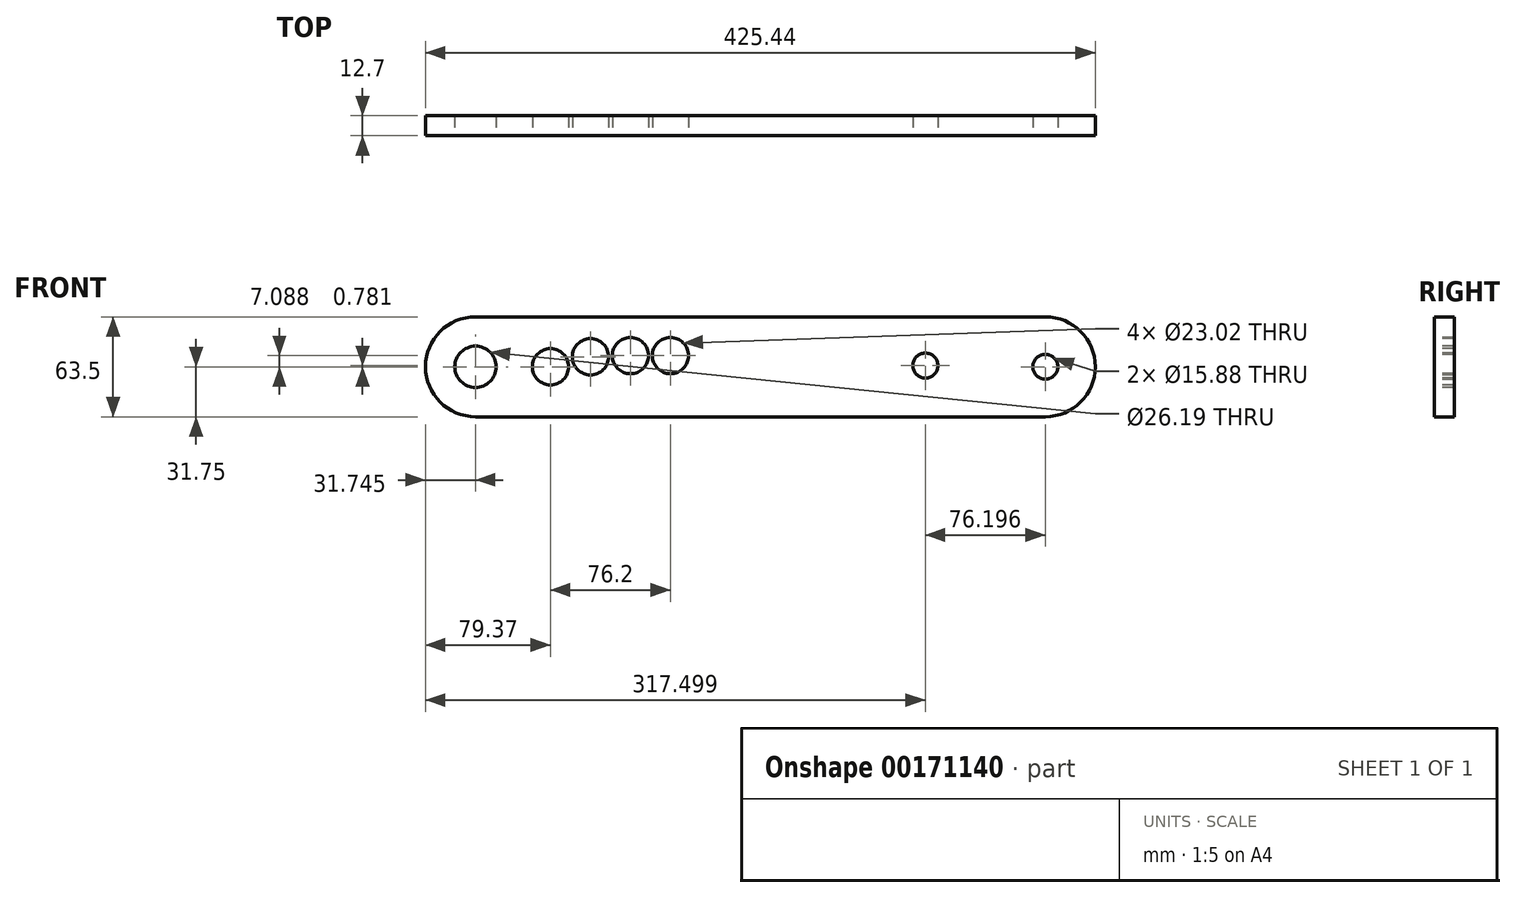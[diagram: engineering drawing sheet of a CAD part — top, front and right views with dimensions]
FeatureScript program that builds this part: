
annotation { "Feature Type Name" : "Feature", "Feature Type Description" : "" }
export const myFeature = defineFeature(function(context is Context, id is Id, definition is map)
    precondition{}
    {
        {
            var Q0;
            Q0=qCreatedBy(makeId("Front.planeOp"),FACE);
            var sketch = newSketch(context, id + "F0", { "sketchPlane" : qUnion([Q0])});
            skLineSegment(sketch, "E0.bottom", {"start": v(-209.55, 44.45) * mm, "end": v(209.55, 44.45) * mm});
            skLineSegment(sketch, "E0.top", {"start": v(-209.55, -44.45) * mm, "end": v(209.55, -44.45) * mm});
            skLineSegment(sketch, "E0.left", {"start": v(-209.55, 44.45) * mm, "end": v(-209.55, -44.45) * mm});
            skLineSegment(sketch, "E0.right", {"start": v(209.55, 44.45) * mm, "end": v(209.55, -44.45) * mm});
            skPoint(sketch, "E0.middle", {"position": v(0, 0) * mm});
            skCircle(sketch, "E1", {"center": v(-177.8, -12.7) * mm, "radius": 13.1 * mm});
            skLineSegment(sketch, "E2", {"start": v(228.8, -12.7) * mm, "end": v(86.37, -12.7) * mm, "construction": true});
            skCircle(sketch, "E3", {"center": v(184.15, -12.7) * mm, "radius": 10.32 * mm});
            skCircle(sketch, "E4", {"center": v(133.35, -12.7) * mm, "radius": 10.32 * mm});
            skLineSegment(sketch, "E5", {"start": v(121.2, -19.05) * mm, "end": v(-51.15, -19.05) * mm, "construction": true});
            skCircle(sketch, "E6", {"center": v(82.55, -19.05) * mm, "radius": 11.5 * mm});
            skCircle(sketch, "E7", {"center": v(50.8, -18.73) * mm, "radius": 11.5 * mm});
            skCircle(sketch, "E8", {"center": v(19.05, -19.18) * mm, "radius": 11.5 * mm});
            skCircle(sketch, "E9", {"center": v(-12.7, -18.73) * mm, "radius": 11.5 * mm});
            skSolve(sketch);
        }
        {
            var Q0;
            Q0=makeQuery(id+"F0.imprint","IMPRINT",FACE,{"disambiguationData":[TD([[makeQuery(id+"F0.imprint","IMPRINT",EDGE,{"derivedFrom":sQuery(id+"F0.wireOp",EDGE,"E0.bottom")}),-1.0]])]});
            extrude(context, id + "F1", {"entities" : qUnion([Q0]), "oppositeDirection" : true, "depth" : 12.7 * mm});
        }
        {
            var Q0;
            Q0=makeQuery(id+"F1.opExtrude","CAP_FACE",FACE,{"disambiguationData":[OSD([sQuery(id+"F0.wireOp",EDGE,"E0.bottom"),sQuery(id+"F0.wireOp",EDGE,"E0.top"),sQuery(id+"F0.wireOp",EDGE,"E0.left"),sQuery(id+"F0.wireOp",EDGE,"E0.right"),sQuery(id+"F0.wireOp",EDGE,"E1"),sQuery(id+"F0.wireOp",EDGE,"E3"),sQuery(id+"F0.wireOp",EDGE,"E4"),sQuery(id+"F0.wireOp",EDGE,"E6"),sQuery(id+"F0.wireOp",EDGE,"E7"),sQuery(id+"F0.wireOp",EDGE,"E8"),sQuery(id+"F0.wireOp",EDGE,"E9")])],"isStart":true});
            var sketch = newSketch(context, id + "F2", { "sketchPlane" : qUnion([Q0])});
            skLineSegment(sketch, "E10", {"start": v(-177.73, 37.77) * mm, "end": v(-177.73, -158.75) * mm, "construction": true});
            skLineSegment(sketch, "E11", {"start": v(-177.8, -12.7) * mm, "end": v(-109.95, -12.7) * mm, "construction": true});
            skLineSegment(sketch, "E12", {"start": v(-177.73, -158.75) * mm, "end": v(-149.16, -158.75) * mm, "construction": true});
            skArc(sketch, "E13", {"start": v(-193.34, 13.47) * mm, "mid": v(-92.02, 9.62) * mm, "end": v(-9.28, -48.99) * mm, "construction": true});
            skCircle(sketch, "E14", {"center": v(-45.76, -14.1) * mm, "radius": 11.5 * mm});
            skCircle(sketch, "E15", {"center": v(-71.52, 1.63) * mm, "radius": 11.5 * mm});
            skCircle(sketch, "E16", {"center": v(-104.3, 14.02) * mm, "radius": 11.5 * mm});
            skCircle(sketch, "E17", {"center": v(-142.08, 18.42) * mm, "radius": 11.5 * mm});
            skSolve(sketch);
        }
        {
            var Q0;
            Q0=makeQuery(id+"F2.imprint","IMPRINT",FACE,{"disambiguationData":[TD([[makeQuery(id+"F2.imprint","IMPRINT",EDGE,{"derivedFrom":sQuery(id+"F2.wireOp",EDGE,"E17")}),1.0]])]});
            var Q1;
            Q1=makeQuery(id+"F2.imprint","IMPRINT",FACE,{"disambiguationData":[TD([[makeQuery(id+"F2.imprint","IMPRINT",EDGE,{"derivedFrom":sQuery(id+"F2.wireOp",EDGE,"E16")}),1.0]])]});
            var Q2;
            Q2=makeQuery(id+"F2.imprint","IMPRINT",FACE,{"disambiguationData":[TD([[makeQuery(id+"F2.imprint","IMPRINT",EDGE,{"derivedFrom":sQuery(id+"F2.wireOp",EDGE,"E15")}),1.0]])]});
            var Q3;
            Q3=makeQuery(id+"F2.imprint","IMPRINT",FACE,{"disambiguationData":[TD([[makeQuery(id+"F2.imprint","IMPRINT",EDGE,{"derivedFrom":sQuery(id+"F2.wireOp",EDGE,"E14")}),1.0]])]});
            extrude(context, id + "F3", {"entities" : qUnion([Q0, Q1, Q2, Q3]), "operationType" : NewBodyOperationType.REMOVE, "endBound" : BoundingType.THROUGH_ALL, "oppositeDirection" : true, "depth" : 25.4 * mm});
        }
        {
            var Q0;
            Q0=makeQuery(id+"F1.opExtrude","CAP_FACE",FACE,{"disambiguationData":[OSD([sQuery(id+"F0.wireOp",EDGE,"E0.bottom"),sQuery(id+"F0.wireOp",EDGE,"E0.top"),sQuery(id+"F0.wireOp",EDGE,"E0.left"),sQuery(id+"F0.wireOp",EDGE,"E0.right"),sQuery(id+"F0.wireOp",EDGE,"E1"),sQuery(id+"F0.wireOp",EDGE,"E3"),sQuery(id+"F0.wireOp",EDGE,"E4"),sQuery(id+"F0.wireOp",EDGE,"E6"),sQuery(id+"F0.wireOp",EDGE,"E7"),sQuery(id+"F0.wireOp",EDGE,"E8"),sQuery(id+"F0.wireOp",EDGE,"E9")])],"isStart":true});
            var sketch = newSketch(context, id + "F4", { "sketchPlane" : qUnion([Q0])});
            skCircle(sketch, "E18", {"center": v(-177.8, -12.7) * mm, "radius": 31.75 * mm});
            skLineSegment(sketch, "E19", {"start": v(-165.1, 44.45) * mm, "end": v(-200.1, 9.9) * mm});
            skLineSegment(sketch, "E20", {"start": v(-146.05, -65.48) * mm, "end": v(-146.05, 3.2) * mm, "construction": true});
            skArc(sketch, "E21", {"start": v(-146.05, -12.7) * mm, "mid": v(-143.4, -4.8) * mm, "end": v(-135.73, -1.54) * mm});
            skFitSpline(sketch, "E22", {"points": [v(-135.73, -1.54) * mm, v(-97.75, -11.51) * mm, v(-55.1, -36.8) * mm, v(-38.1, -44.45) * mm], "startDerivative": vector(106.71, -14.43) * mm, "endDerivative": vector(80.2, -15.75) * mm});
            skSolve(sketch);
        }
        {
            var Q0;
            {var subQ0=sQuery(id+"F4.wireOp",EDGE,"E19");Q0=makeQuery(id+"F4.imprint","IMPRINT",FACE,{"disambiguationData":[TD([[makeQuery(id+"F4.imprint","IMPRINT",EDGE,{"derivedFrom":subQ0}),-1.0]])]});}
            var Q1;
            {var subQ0=sQuery(id+"F4.wireOp",EDGE,"E18");var subQ1=makeQuery(id+"F1.opExtrude","CAP_EDGE",EDGE,{"disambiguationData":[OSD([sQuery(id+"F0.wireOp",EDGE,"E0.left")])],"isStart":true});var subQ2=makeQuery(id+"F4.imprint","INTERSECT",VERTEX,{"derivedFrom":[subQ1,subQ0]});Q1=makeQuery(id+"F4.imprint","IMPRINT",FACE,{"disambiguationData":[TD([[makeQuery(id+"F4.imprint","IMPRINT",EDGE,{"disambiguationData":[TD([[subQ2,-1.0]])],"derivedFrom":subQ0}),-1.0]])]});}
            var Q2;
            {var subQ0=sQuery(id+"F4.wireOp",EDGE,"E22");Q2=makeQuery(id+"F4.imprint","IMPRINT",FACE,{"disambiguationData":[TD([[makeQuery(id+"F4.imprint","IMPRINT",EDGE,{"derivedFrom":subQ0}),-1.0]])]});}
            extrude(context, id + "F5", {"entities" : qUnion([Q0, Q1, Q2]), "operationType" : NewBodyOperationType.REMOVE, "endBound" : BoundingType.THROUGH_ALL, "oppositeDirection" : true, "depth" : 25.4 * mm});
        }
        {
            var Q0;
            Q0=makeQuery(id+"F1.opExtrude","CAP_FACE",FACE,{"disambiguationData":[OSD([sQuery(id+"F0.wireOp",EDGE,"E0.bottom"),sQuery(id+"F0.wireOp",EDGE,"E0.top"),sQuery(id+"F0.wireOp",EDGE,"E0.left"),sQuery(id+"F0.wireOp",EDGE,"E0.right"),sQuery(id+"F0.wireOp",EDGE,"E1"),sQuery(id+"F0.wireOp",EDGE,"E3"),sQuery(id+"F0.wireOp",EDGE,"E4"),sQuery(id+"F0.wireOp",EDGE,"E6"),sQuery(id+"F0.wireOp",EDGE,"E7"),sQuery(id+"F0.wireOp",EDGE,"E8"),sQuery(id+"F0.wireOp",EDGE,"E9")])],"isStart":true});
            var sketch = newSketch(context, id + "F6", { "sketchPlane" : qUnion([Q0])});
            skLineSegment(sketch, "E23", {"start": v(163.51, 44.45) * mm, "end": v(202.25, 5.12) * mm});
            skArc(sketch, "E24", {"start": v(199.4, -33.02) * mm, "mid": v(209.48, -14.6) * mm, "end": v(202.25, 5.12) * mm});
            skLineSegment(sketch, "E25", {"start": v(184.15, -44.45) * mm, "end": v(199.4, -33.02) * mm});
            skSolve(sketch);
        }
        {
            var Q0;
            {var subQ0=sQuery(id+"F6.wireOp",EDGE,"E23");Q0=makeQuery(id+"F6.imprint","IMPRINT",FACE,{"disambiguationData":[TD([[makeQuery(id+"F6.imprint","IMPRINT",EDGE,{"derivedFrom":subQ0}),1.0]])]});}
            var Q1;
            {var subQ0=sQuery(id+"F6.wireOp",EDGE,"E25");Q1=makeQuery(id+"F6.imprint","IMPRINT",FACE,{"disambiguationData":[TD([[makeQuery(id+"F6.imprint","IMPRINT",EDGE,{"derivedFrom":subQ0}),-1.0]])]});}
            extrude(context, id + "F7", {"entities" : qUnion([Q0, Q1]), "operationType" : NewBodyOperationType.REMOVE, "endBound" : BoundingType.THROUGH_ALL, "oppositeDirection" : true, "depth" : 25.4 * mm});
        }
        {
            var Q0;
            Q0=qCreatedBy(makeId("Front.planeOp"),FACE);
            var sketch = newSketch(context, id + "F8", { "sketchPlane" : qUnion([Q0])});
            skLineSegment(sketch, "E26.bottom", {"start": v(-180.98, 31.75) * mm, "end": v(180.97, 31.75) * mm});
            skLineSegment(sketch, "E26.top", {"start": v(-180.98, -31.75) * mm, "end": v(180.97, -31.75) * mm});
            skPoint(sketch, "E26.middle", {"position": v(0, 0) * mm});
            skArc(sketch, "E27", {"start": v(-180.98, 31.75) * mm, "mid": v(-212.73, 0) * mm, "end": v(-180.98, -31.75) * mm});
            skArc(sketch, "E28", {"start": v(180.98, -31.75) * mm, "mid": v(212.73, 0) * mm, "end": v(180.98, 31.75) * mm});
            skPoint(sketch, "E29.orphan", {"position": v(-212.73, 31.75) * mm});
            skPoint(sketch, "E30.orphan", {"position": v(-212.73, -31.75) * mm});
            skPoint(sketch, "E31.orphan", {"position": v(212.72, 31.75) * mm});
            skPoint(sketch, "E32.orphan", {"position": v(212.72, -31.75) * mm});
            skSolve(sketch);
        }
        {
            var Q0;
            Q0=makeQuery(id+"F8.imprint","IMPRINT",FACE,{"disambiguationData":[TD([[makeQuery(id+"F8.imprint","IMPRINT",EDGE,{"derivedFrom":sQuery(id+"F8.wireOp",EDGE,"E26.bottom")}),-1.0]])]});
            extrude(context, id + "F9", {"entities" : qUnion([Q0]), "depth" : 12.7 * mm});
        }
        {
            var Q0;
            Q0=makeQuery(id+"F9.opExtrude","CAP_FACE",FACE,{"disambiguationData":[OSD([sQuery(id+"F8.wireOp",EDGE,"E26.bottom"),sQuery(id+"F8.wireOp",EDGE,"E26.top"),sQuery(id+"F8.wireOp",EDGE,"E27"),sQuery(id+"F8.wireOp",EDGE,"E28")])],"isStart":false});
            var sketch = newSketch(context, id + "F10", { "sketchPlane" : qUnion([Q0])});
            skCircle(sketch, "E33", {"center": v(-180.98, 0) * mm, "radius": 13.1 * mm});
            skCircle(sketch, "E34", {"center": v(-133.35, 0) * mm, "radius": 11.5 * mm});
            skLineSegment(sketch, "E35", {"start": v(-115.23, 6.35) * mm, "end": v(-36.78, 6.35) * mm, "construction": true});
            skCircle(sketch, "E36", {"center": v(-107.95, 6.35) * mm, "radius": 11.5 * mm});
            skCircle(sketch, "E37", {"center": v(-82.55, 7.09) * mm, "radius": 11.5 * mm});
            skCircle(sketch, "E38", {"center": v(-57.15, 7.09) * mm, "radius": 11.5 * mm});
            skCircle(sketch, "E39", {"center": v(180.98, 0) * mm, "radius": 7.94 * mm});
            skCircle(sketch, "E40", {"center": v(104.78, 0.78) * mm, "radius": 7.94 * mm});
            skSolve(sketch);
        }
        {
            var Q0;
            Q0=makeQuery(id+"F10.imprint","IMPRINT",FACE,{"disambiguationData":[TD([[makeQuery(id+"F10.imprint","IMPRINT",EDGE,{"derivedFrom":sQuery(id+"F10.wireOp",EDGE,"E33")}),1.0]])]});
            var Q1;
            Q1=makeQuery(id+"F10.imprint","IMPRINT",FACE,{"disambiguationData":[TD([[makeQuery(id+"F10.imprint","IMPRINT",EDGE,{"derivedFrom":sQuery(id+"F10.wireOp",EDGE,"E34")}),1.0]])]});
            var Q2;
            Q2=makeQuery(id+"F10.imprint","IMPRINT",FACE,{"disambiguationData":[TD([[makeQuery(id+"F10.imprint","IMPRINT",EDGE,{"derivedFrom":sQuery(id+"F10.wireOp",EDGE,"E36")}),1.0]])]});
            var Q3;
            Q3=makeQuery(id+"F10.imprint","IMPRINT",FACE,{"disambiguationData":[TD([[makeQuery(id+"F10.imprint","IMPRINT",EDGE,{"derivedFrom":sQuery(id+"F10.wireOp",EDGE,"E37")}),1.0]])]});
            var Q4;
            Q4=makeQuery(id+"F10.imprint","IMPRINT",FACE,{"disambiguationData":[TD([[makeQuery(id+"F10.imprint","IMPRINT",EDGE,{"derivedFrom":sQuery(id+"F10.wireOp",EDGE,"E38")}),1.0]])]});
            var Q5;
            Q5=makeQuery(id+"F10.imprint","IMPRINT",FACE,{"disambiguationData":[TD([[makeQuery(id+"F10.imprint","IMPRINT",EDGE,{"derivedFrom":sQuery(id+"F10.wireOp",EDGE,"E40")}),1.0]])]});
            var Q6;
            Q6=makeQuery(id+"F10.imprint","IMPRINT",FACE,{"disambiguationData":[TD([[makeQuery(id+"F10.imprint","IMPRINT",EDGE,{"derivedFrom":sQuery(id+"F10.wireOp",EDGE,"E39")}),1.0]])]});
            extrude(context, id + "F11", {"entities" : qUnion([Q0, Q1, Q2, Q3, Q4, Q5, Q6]), "operationType" : NewBodyOperationType.REMOVE, "endBound" : BoundingType.THROUGH_ALL, "oppositeDirection" : true, "depth" : 25.4 * mm});
        }
        {
            var Q0;
            Q0=makeQuery(id+"F1.opExtrude","SWEPT_BODY",BODY,{"disambiguationData":[OSD([sQuery(id+"F0.wireOp",EDGE,"E0.bottom"),sQuery(id+"F0.wireOp",EDGE,"E0.top"),sQuery(id+"F0.wireOp",EDGE,"E0.left"),sQuery(id+"F0.wireOp",EDGE,"E0.right"),sQuery(id+"F0.wireOp",EDGE,"E1"),sQuery(id+"F0.wireOp",EDGE,"E3"),sQuery(id+"F0.wireOp",EDGE,"E4"),sQuery(id+"F0.wireOp",EDGE,"E6"),sQuery(id+"F0.wireOp",EDGE,"E7"),sQuery(id+"F0.wireOp",EDGE,"E8"),sQuery(id+"F0.wireOp",EDGE,"E9")])]});
            deleteBodies(context, id + "F12", {"entities" : qUnion([Q0])});
        }
    });
